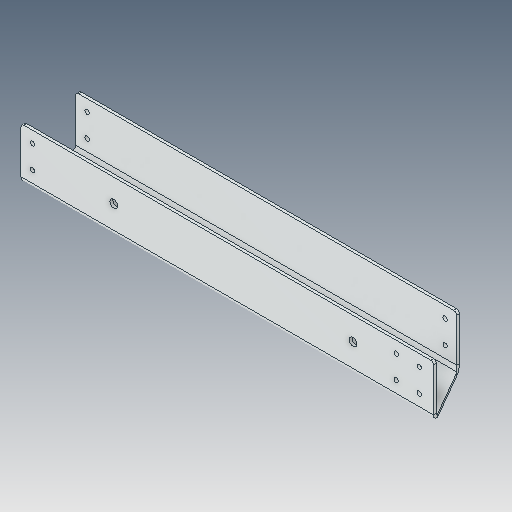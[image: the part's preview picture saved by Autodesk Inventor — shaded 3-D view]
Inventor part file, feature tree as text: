
AUTODESK INVENTOR PART (.ipt)
format: ipt  version: 2023.5 (Build 275446000, 446)  size: 137,728 bytes
history: native  units: in
note: dims shown in document units (in); Inventor stores cm internally (conversion verified against a paired STEP export)
features: fillet x1
ambient origin geometry x8: Origin, YZ Plane, XZ Plane, XY Plane, X Axis, Y Axis, Z Axis, Center Point
bodies: Solid1 (feature_tree)
feature tree (1):
  fillet  "Fillet1"  [1 undecoded]
note: 1 required parameter value undecoded (feature->parameter linkage not recoverable at this tier; creation-order binding heuristic only, values carry confidence <= 0.55)
